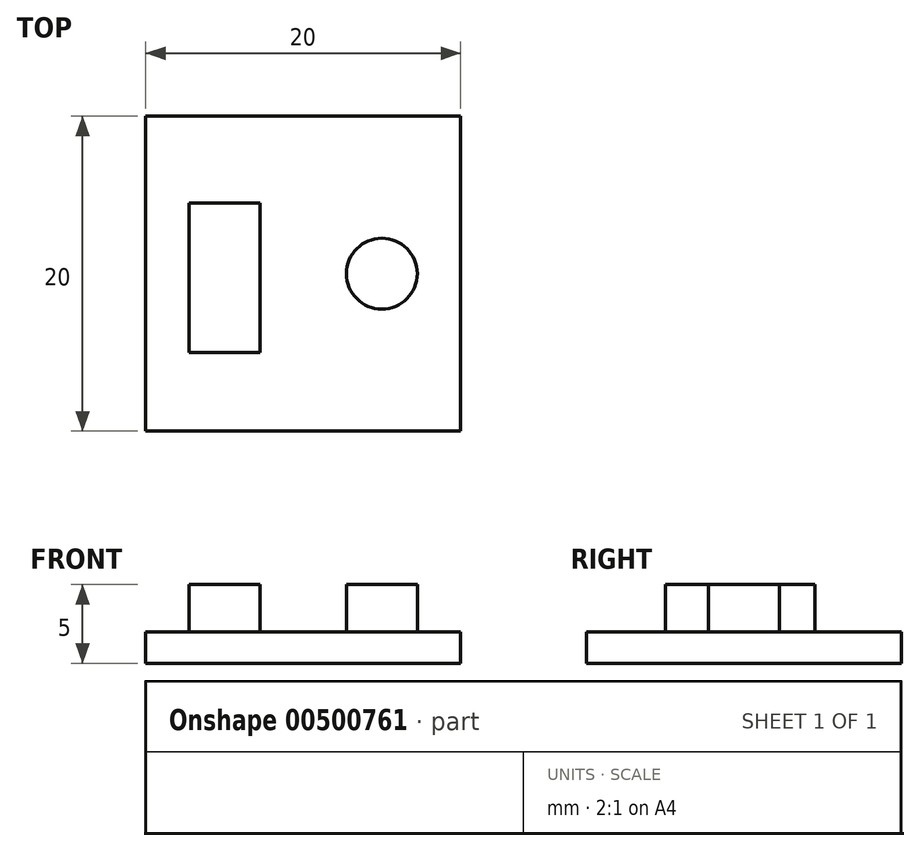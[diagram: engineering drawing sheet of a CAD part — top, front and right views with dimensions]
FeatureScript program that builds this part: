
annotation { "Feature Type Name" : "Feature", "Feature Type Description" : "" }
export const myFeature = defineFeature(function(context is Context, id is Id, definition is map)
    precondition{}
    {
        {
            var Q0;
            Q0=qCreatedBy(makeId("Top.planeOp"),FACE);
            var sketch = newSketch(context, id + "F0", { "sketchPlane" : qUnion([Q0])});
            skLineSegment(sketch, "E0.bottom", {"start": v(-10, 10) * mm, "end": v(10, 10) * mm});
            skLineSegment(sketch, "E0.top", {"start": v(-10, -10) * mm, "end": v(10, -10) * mm});
            skLineSegment(sketch, "E0.left", {"start": v(-10, 10) * mm, "end": v(-10, -10) * mm});
            skLineSegment(sketch, "E0.right", {"start": v(10, 10) * mm, "end": v(10, -10) * mm});
            skLineSegment(sketch, "E1.bottom", {"start": v(-7.25, 4.5) * mm, "end": v(-2.75, 4.5) * mm});
            skLineSegment(sketch, "E1.top", {"start": v(-7.25, -5) * mm, "end": v(-2.75, -5) * mm});
            skLineSegment(sketch, "E1.left", {"start": v(-7.25, 4.5) * mm, "end": v(-7.25, -5) * mm});
            skLineSegment(sketch, "E1.right", {"start": v(-2.75, 4.5) * mm, "end": v(-2.75, -5) * mm});
            skCircle(sketch, "E2", {"center": v(5, 0) * mm, "radius": 2.25 * mm});
            skSolve(sketch);
        }
        {
            var Q0;
            Q0=makeQuery(id+"F0.imprint","IMPRINT",FACE,{"disambiguationData":[TD([[makeQuery(id+"F0.imprint","IMPRINT",EDGE,{"derivedFrom":sQuery(id+"F0.wireOp",EDGE,"E0.bottom")}),-1.0]])]});
            extrude(context, id + "F1", {"entities" : qUnion([Q0]), "depth" : 2 * mm});
        }
        {
            var Q0;
            Q0=makeQuery(id+"F0.imprint","IMPRINT",FACE,{"disambiguationData":[TD([[makeQuery(id+"F0.imprint","IMPRINT",EDGE,{"derivedFrom":sQuery(id+"F0.wireOp",EDGE,"E1.bottom")}),-1.0]])]});
            var Q1;
            Q1=makeQuery(id+"F0.imprint","IMPRINT",FACE,{"disambiguationData":[TD([[makeQuery(id+"F0.imprint","IMPRINT",EDGE,{"derivedFrom":sQuery(id+"F0.wireOp",EDGE,"E2")}),1.0]])]});
            extrude(context, id + "F2", {"entities" : qUnion([Q0, Q1]), "operationType" : NewBodyOperationType.ADD, "depth" : 5 * mm});
        }
    });
